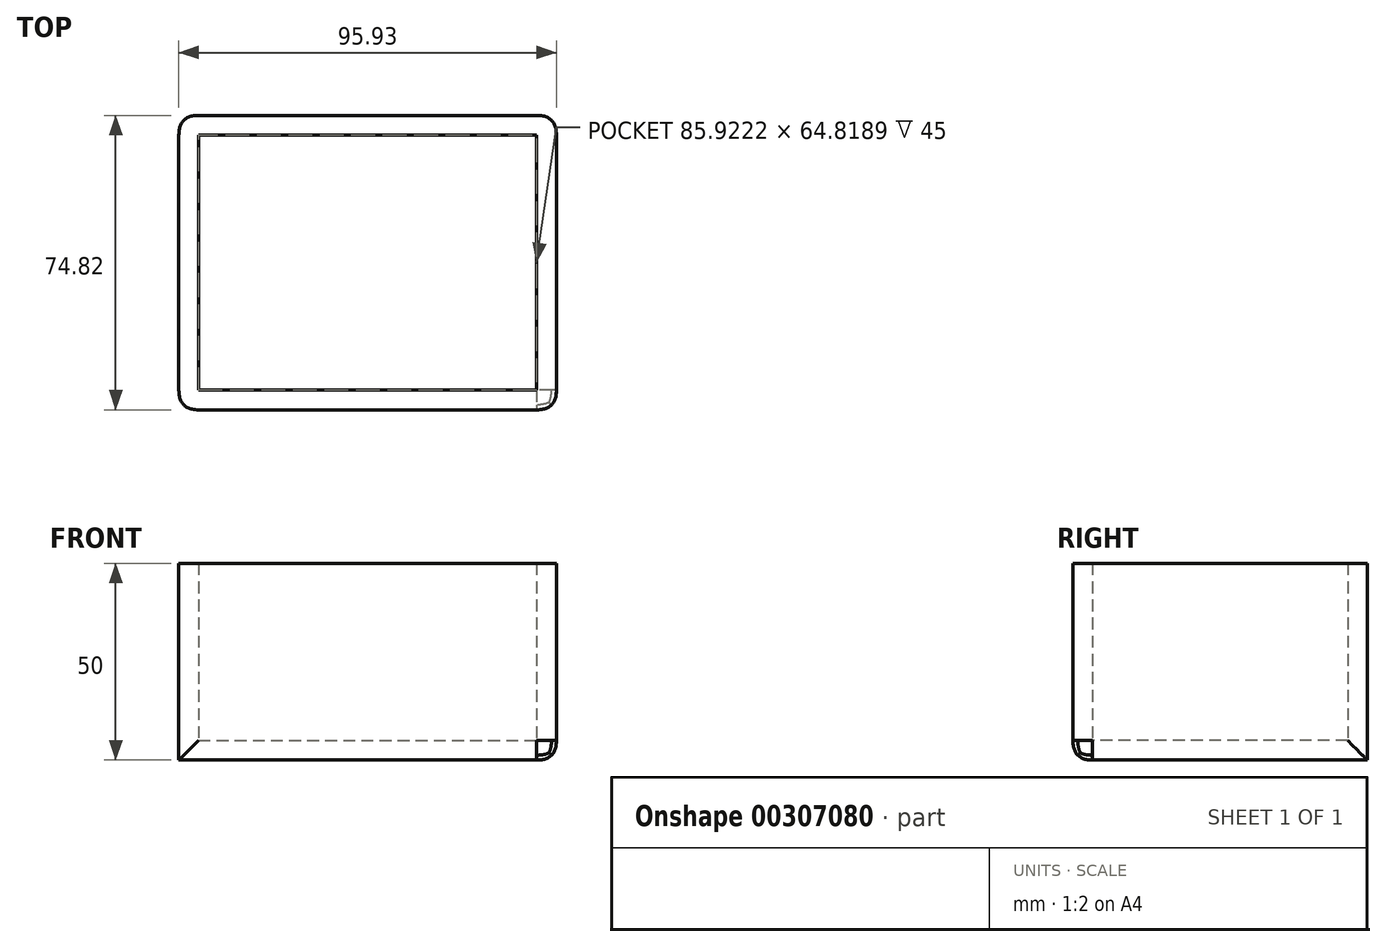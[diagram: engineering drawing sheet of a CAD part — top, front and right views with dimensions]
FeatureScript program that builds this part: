
annotation { "Feature Type Name" : "Feature", "Feature Type Description" : "" }
export const myFeature = defineFeature(function(context is Context, id is Id, definition is map)
    precondition{}
    {
        {
            var Q0;
            Q0=qCreatedBy(makeId("Top.planeOp"),FACE);
            var sketch = newSketch(context, id + "F0", { "sketchPlane" : qUnion([Q0])});
            skLineSegment(sketch, "E0.bottom", {"start": v(-36.22, 25.6) * mm, "end": v(59.7, 25.6) * mm});
            skLineSegment(sketch, "E0.top", {"start": v(-36.22, -49.22) * mm, "end": v(59.7, -49.22) * mm});
            skLineSegment(sketch, "E0.left", {"start": v(-36.22, 25.6) * mm, "end": v(-36.22, -49.22) * mm});
            skLineSegment(sketch, "E0.right", {"start": v(59.7, 25.6) * mm, "end": v(59.7, -49.22) * mm});
            skSolve(sketch);
        }
        {
            var Q0;
            Q0=makeQuery(id+"F0.imprint","IMPRINT",FACE,{"disambiguationData":[TD([[makeQuery(id+"F0.imprint","IMPRINT",EDGE,{"derivedFrom":sQuery(id+"F0.wireOp",EDGE,"E0.bottom")}),-1.0]])]});
            extrude(context, id + "F1", {"entities" : qUnion([Q0]), "depth" : 50 * mm});
        }
        {
            var Q0;
            Q0=makeQuery(id+"F1.opExtrude","CAP_FACE",FACE,{"disambiguationData":[OSD([sQuery(id+"F0.wireOp",EDGE,"E0.bottom"),sQuery(id+"F0.wireOp",EDGE,"E0.top"),sQuery(id+"F0.wireOp",EDGE,"E0.left"),sQuery(id+"F0.wireOp",EDGE,"E0.right")])],"isStart":false});
            shell(context, id + "F2", {"entities" : qUnion([Q0]), "thickness" : 5 * mm});
        }
        {
            var Q0;
            Q0=makeQuery(id+"F1.opExtrude","SWEPT_EDGE",EDGE,{"disambiguationData":[OSD([sQuery(id+"F0.wireOp",EDGE,"E0.top"),sQuery(id+"F0.wireOp",EDGE,"E0.left")])]});
            var Q1;
            Q1=makeQuery(id+"F1.opExtrude","SWEPT_EDGE",EDGE,{"disambiguationData":[OSD([sQuery(id+"F0.wireOp",EDGE,"E0.top"),sQuery(id+"F0.wireOp",EDGE,"E0.right")])]});
            var Q2;
            Q2=makeQuery(id+"F1.opExtrude","CAP_EDGE",EDGE,{"disambiguationData":[OSD([sQuery(id+"F0.wireOp",EDGE,"E0.right")])],"isStart":true});
            var Q3;
            Q3=makeQuery(id+"F1.opExtrude","CAP_EDGE",EDGE,{"disambiguationData":[OSD([sQuery(id+"F0.wireOp",EDGE,"E0.top")])],"isStart":true});
            var Q4;
            Q4=makeQuery(id+"F1.opExtrude","SWEPT_EDGE",EDGE,{"disambiguationData":[OSD([sQuery(id+"F0.wireOp",EDGE,"E0.bottom"),sQuery(id+"F0.wireOp",EDGE,"E0.right")])]});
            var Q5;
            Q5=makeQuery(id+"F1.opExtrude","SWEPT_EDGE",EDGE,{"disambiguationData":[OSD([sQuery(id+"F0.wireOp",EDGE,"E0.bottom"),sQuery(id+"F0.wireOp",EDGE,"E0.left")])]});
            fillet(context, id + "F3", {"entities" : qUnion([Q0, Q1, Q2, Q3, Q4, Q5]), "radius" : 5 * mm, "tangentPropagation" : true, "rho" : 0.5, "crossSection" : FilletCrossSection.CONIC, "allowEdgeOverflow" : false});
        }
    });
